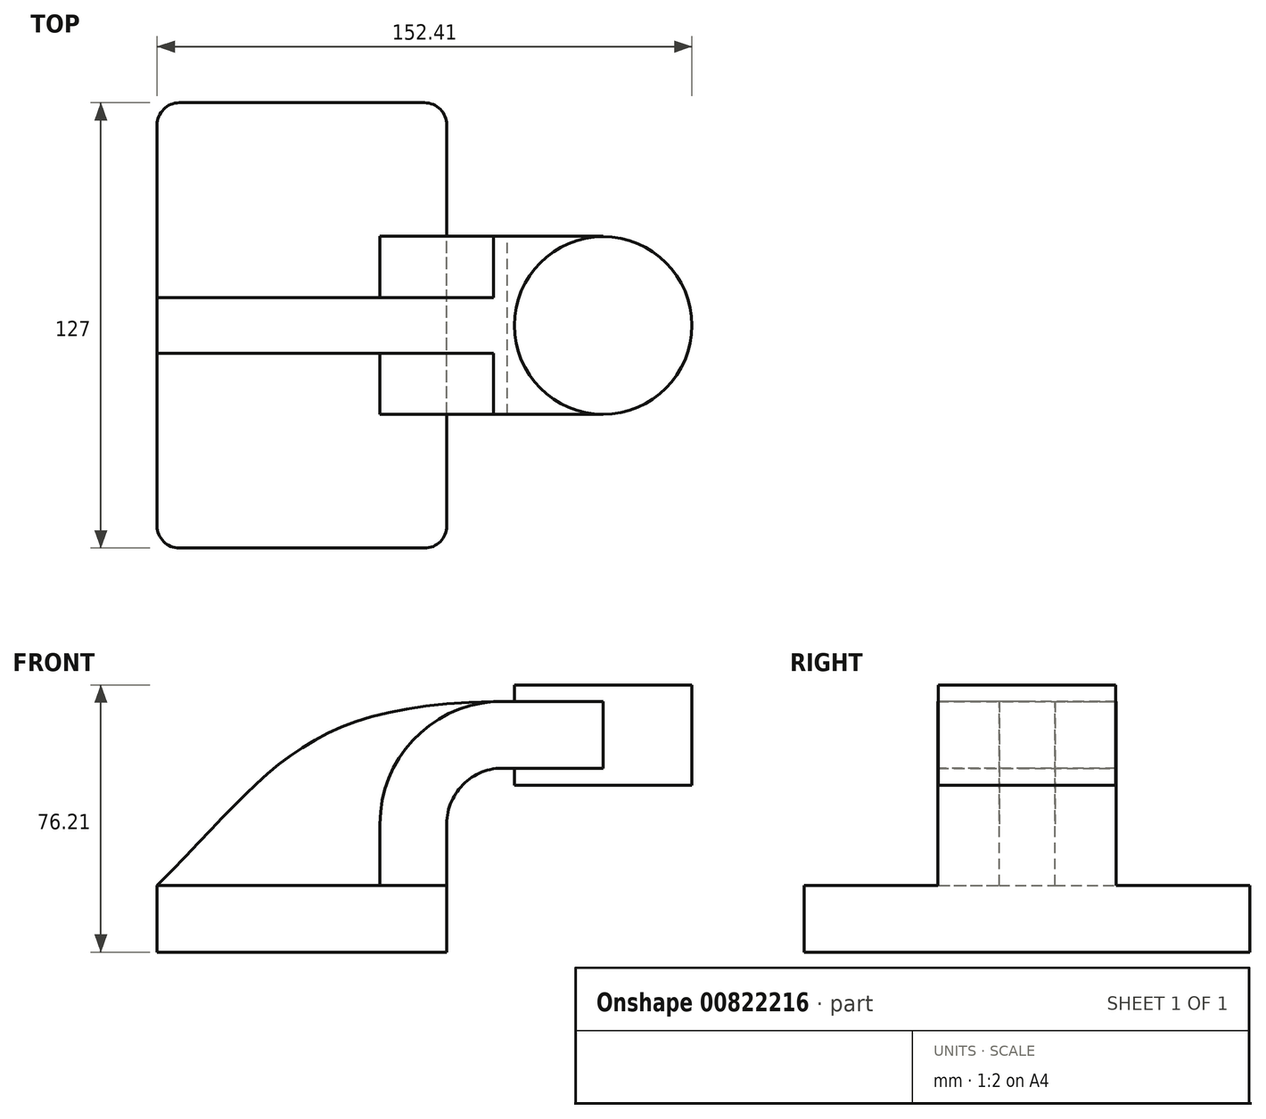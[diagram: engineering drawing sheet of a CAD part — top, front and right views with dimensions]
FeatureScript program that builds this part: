
annotation { "Feature Type Name" : "Feature", "Feature Type Description" : "" }
export const myFeature = defineFeature(function(context is Context, id is Id, definition is map)
    precondition{}
    {
        {
            var Q0;
            Q0=qCreatedBy(makeId("Front.planeOp"),FACE);
            var sketch = newSketch(context, id + "F0", { "sketchPlane" : qUnion([Q0])});
            skLineSegment(sketch, "E0.bottom", {"start": v(41.27, 9.53) * mm, "end": v(-41.28, 9.53) * mm});
            skLineSegment(sketch, "E0.top", {"start": v(41.28, -9.52) * mm, "end": v(-41.27, -9.52) * mm});
            skLineSegment(sketch, "E0.left", {"start": v(41.28, 9.53) * mm, "end": v(41.28, -9.52) * mm});
            skLineSegment(sketch, "E0.right", {"start": v(-41.28, 9.53) * mm, "end": v(-41.27, -9.52) * mm});
            skPoint(sketch, "E0.middle", {"position": v(0, 0) * mm});
            skLineSegment(sketch, "E1.bottom", {"start": v(111.13, 66.68) * mm, "end": v(60.33, 66.68) * mm});
            skLineSegment(sketch, "E1.top", {"start": v(111.13, 38.1) * mm, "end": v(60.33, 38.1) * mm});
            skLineSegment(sketch, "E1.left", {"start": v(111.13, 66.68) * mm, "end": v(111.13, 38.1) * mm});
            skLineSegment(sketch, "E1.right", {"start": v(60.33, 66.68) * mm, "end": v(60.33, 38.1) * mm});
            skPoint(sketch, "E1.middle", {"position": v(85.73, 52.39) * mm});
            skLineSegment(sketch, "E2", {"start": v(41.27, 9.53) * mm, "end": v(41.27, 27.06) * mm});
            skArc(sketch, "E3", {"start": v(41.27, 27.06) * mm, "mid": v(46.42, 38.75) * mm, "end": v(58.5, 42.88) * mm});
            skLineSegment(sketch, "E4", {"start": v(58.5, 42.88) * mm, "end": v(85.82, 42.88) * mm});
            skLineSegment(sketch, "E5.0", {"start": v(59.17, 61.93) * mm, "end": v(85.82, 61.93) * mm});
            skArc(sketch, "E5.1", {"start": v(22.23, 27.06) * mm, "mid": v(33.18, 52.46) * mm, "end": v(59.17, 61.93) * mm});
            skLineSegment(sketch, "E5.2", {"start": v(22.22, 9.53) * mm, "end": v(22.22, 27.06) * mm});
            skLineSegment(sketch, "E6", {"start": v(85.82, 38.1) * mm, "end": v(85.82, 66.68) * mm});
            skFitSpline(sketch, "E7", {"points": [v(-41.28, 9.53) * mm, v(59.17, 61.93) * mm], "startDerivative": vector(101.4, 101.08) * mm, "endDerivative": vector(177.5, 0) * mm});
            skPoint(sketch, "E8", {"position": v(72.5, 61.93) * mm});
            skSolve(sketch);
        }
        {
            var Q0;
            Q0=makeQuery(id+"F0.imprint","IMPRINT",FACE,{"disambiguationData":[TD([[makeQuery(id+"F0.imprint","IMPRINT",EDGE,{"derivedFrom":sQuery(id+"F0.wireOp",EDGE,"E0.top")}),-1.0]])]});
            extrude(context, id + "F1", {"entities" : qUnion([Q0]), "endBound" : BoundingType.SYMMETRIC, "depth" : 127 * mm, "offsetDistance" : 25.4 * mm});
        }
        {
            var Q0;
            {var subQ1=sQuery(id+"F0.wireOp",EDGE,"E2");Q0=makeQuery(id+"F0.imprint","IMPRINT",FACE,{"disambiguationData":[TD([[makeQuery(id+"F0.imprint","IMPRINT",EDGE,{"derivedFrom":subQ1}),1.0]])]});}
            extrude(context, id + "F2", {"entities" : qUnion([Q0]), "operationType" : NewBodyOperationType.ADD, "endBound" : BoundingType.SYMMETRIC, "depth" : 50.8 * mm, "offsetDistance" : 25.4 * mm});
        }
        {
            var Q0;
            {var subQ3=sQuery(id+"F0.wireOp",EDGE,"E5.2");Q0=makeQuery(id+"F0.imprint","IMPRINT",FACE,{"disambiguationData":[TD([[makeQuery(id+"F0.imprint","IMPRINT",EDGE,{"derivedFrom":subQ3}),1.0]])]});}
            extrude(context, id + "F3", {"entities" : qUnion([Q0]), "operationType" : NewBodyOperationType.ADD, "endBound" : BoundingType.SYMMETRIC, "depth" : 15.88 * mm, "offsetDistance" : 25.4 * mm});
        }
        {
            var Q0;
            {var subQ0=sQuery(id+"F0.wireOp",EDGE,"E5.0");var subQ1=sQuery(id+"F0.wireOp",EDGE,"E1.right");var subQ2=makeQuery(id+"F0.imprint","INTERSECT",VERTEX,{"derivedFrom":[subQ1,subQ0]});Q0=makeQuery(id+"F0.imprint","IMPRINT",FACE,{"disambiguationData":[TD([[makeQuery(id+"F0.imprint","IMPRINT",EDGE,{"disambiguationData":[TD([[subQ2,-1.0]])],"derivedFrom":subQ1}),1.0]])]});}
            extrude(context, id + "F4", {"entities" : qUnion([Q0]), "operationType" : NewBodyOperationType.ADD, "endBound" : BoundingType.SYMMETRIC, "depth" : 50.8 * mm, "offsetDistance" : 25.4 * mm});
        }
        {
            var Q0;
            {var subQ0=sQuery(id+"F0.wireOp",EDGE,"E1.left");Q0=makeQuery(id+"F0.imprint","IMPRINT",FACE,{"disambiguationData":[TD([[makeQuery(id+"F0.imprint","IMPRINT",EDGE,{"derivedFrom":subQ0}),-1.0]])]});}
            var Q1;
            Q1=sQuery(id+"F0.wireOp",EDGE,"E6");
            revolve(context, id + "F5", {"operationType" : NewBodyOperationType.ADD, "surfaceOperationType" : NewSurfaceOperationType.NEW, "entities" : qUnion([Q0]), "axis" : qUnion([Q1]), "revolveType" : RevolveType.FULL});
        }
        {
            var Q0;
            Q0=makeQuery(id+"F1.opExtrude","CAP_EDGE",EDGE,{"disambiguationData":[OSD([sQuery(id+"F0.wireOp",EDGE,"E0.left")])],"isStart":false});
            var Q1;
            Q1=makeQuery(id+"F1.opExtrude","CAP_EDGE",EDGE,{"disambiguationData":[OSD([sQuery(id+"F0.wireOp",EDGE,"E0.right")])],"isStart":false});
            var Q2;
            Q2=makeQuery(id+"F1.opExtrude","CAP_EDGE",EDGE,{"disambiguationData":[OSD([sQuery(id+"F0.wireOp",EDGE,"E0.left")])],"isStart":true});
            var Q3;
            Q3=makeQuery(id+"F1.opExtrude","CAP_EDGE",EDGE,{"disambiguationData":[OSD([sQuery(id+"F0.wireOp",EDGE,"E0.right")])],"isStart":true});
            fillet(context, id + "F6", {"entities" : qUnion([Q0, Q1, Q2, Q3]), "radius" : 6.35 * mm, "tangentPropagation" : true, "allowEdgeOverflow" : false});
        }
    });
